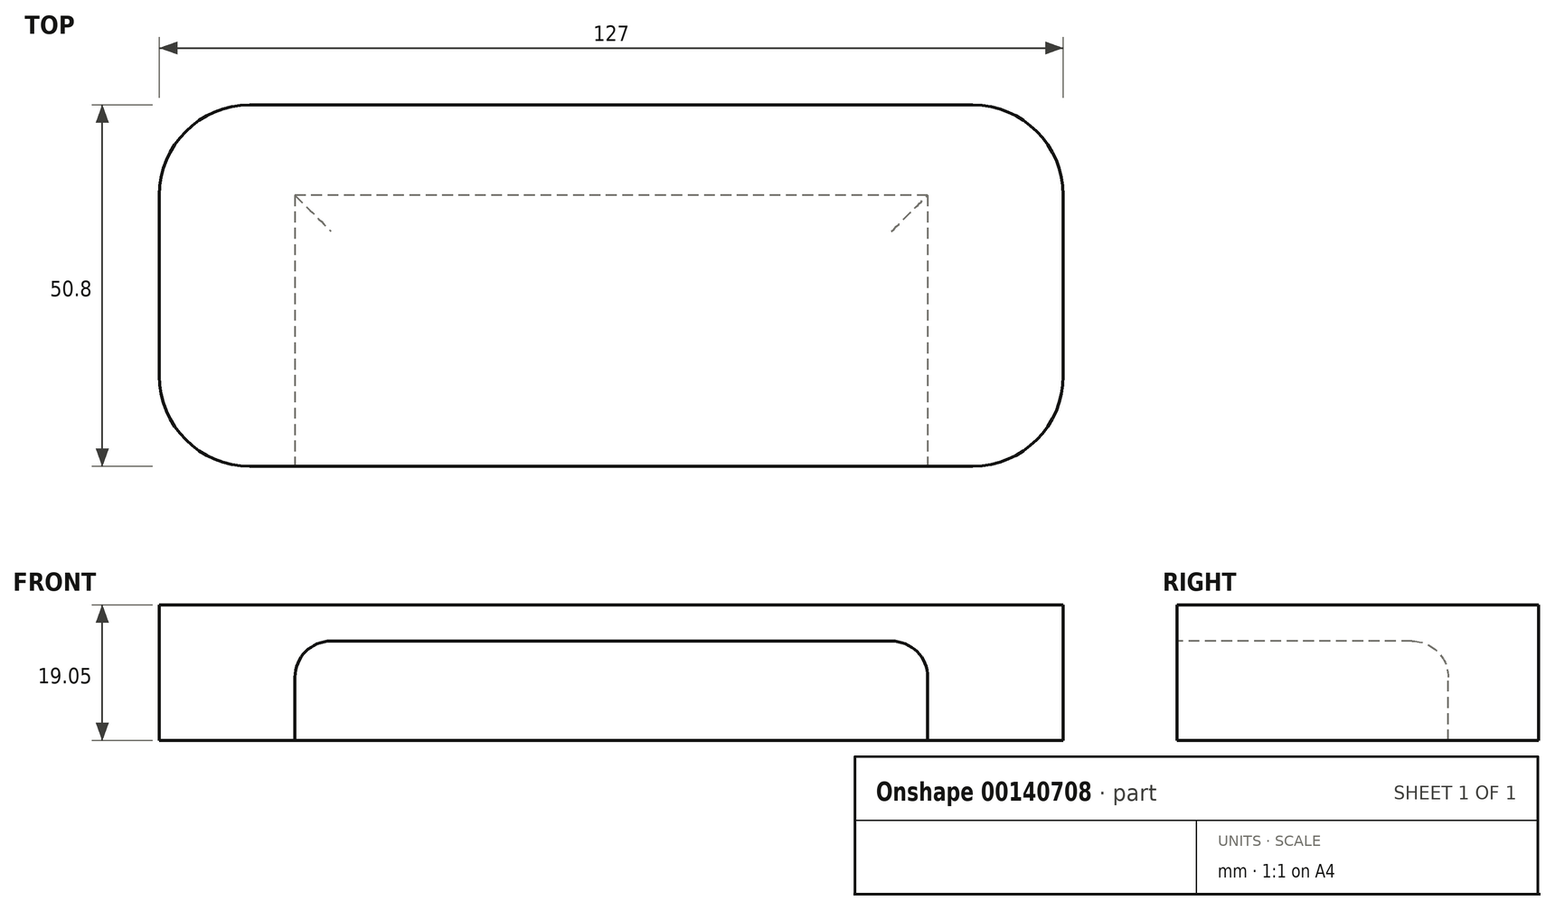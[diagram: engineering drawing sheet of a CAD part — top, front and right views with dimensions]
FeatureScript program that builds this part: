
annotation { "Feature Type Name" : "Feature", "Feature Type Description" : "" }
export const myFeature = defineFeature(function(context is Context, id is Id, definition is map)
    precondition{}
    {
        {
            var Q0;
            Q0=qCreatedBy(makeId("Top.planeOp"),FACE);
            var sketch = newSketch(context, id + "F0", { "sketchPlane" : qUnion([Q0])});
            skLineSegment(sketch, "E0.bottom", {"start": v(63.5, 25.4) * mm, "end": v(-63.5, 25.4) * mm});
            skLineSegment(sketch, "E0.top", {"start": v(63.5, -25.4) * mm, "end": v(-63.5, -25.4) * mm});
            skLineSegment(sketch, "E0.left", {"start": v(63.5, 25.4) * mm, "end": v(63.5, -25.4) * mm});
            skLineSegment(sketch, "E0.right", {"start": v(-63.5, 25.4) * mm, "end": v(-63.5, -25.4) * mm});
            skPoint(sketch, "E0.middle", {"position": v(0, 0) * mm});
            skSolve(sketch);
        }
        {
            var Q0;
            Q0 = qSketchRegion(id + "F0", true);
            extrude(context, id + "F1", {"entities" : qUnion([Q0]), "depth" : 19.05 * mm});
        }
        {
            var Q0;
            Q0=makeQuery(id+"F1.opExtrude","SWEPT_FACE",FACE,{"disambiguationData":[OSD([sQuery(id+"F0.wireOp",EDGE,"E0.top")])]});
            var sketch = newSketch(context, id + "F2", { "sketchPlane" : qUnion([Q0])});
            skLineSegment(sketch, "E1.bottom", {"start": v(-44.45, 0) * mm, "end": v(44.45, 0) * mm});
            skLineSegment(sketch, "E1.top", {"start": v(-44.45, 13.97) * mm, "end": v(44.45, 13.97) * mm});
            skLineSegment(sketch, "E1.left", {"start": v(-44.45, 0) * mm, "end": v(-44.45, 13.97) * mm});
            skLineSegment(sketch, "E1.right", {"start": v(44.45, 0) * mm, "end": v(44.45, 13.97) * mm});
            skSolve(sketch);
        }
        {
            var Q0;
            Q0 = qSketchRegion(id + "F2", true);
            extrude(context, id + "F3", {"entities" : qUnion([Q0]), "operationType" : NewBodyOperationType.REMOVE, "oppositeDirection" : true, "depth" : 38.1 * mm});
        }
        {
            var Q0;
            Q0=makeQuery(id+"F3.boolean.opBoolean","COPY",EDGE,{"derivedFrom":makeQuery(id+"F3.opExtrude","SWEPT_EDGE",EDGE,{"disambiguationData":[OSD([sQuery(id+"F2.wireOp",EDGE,"E1.top"),sQuery(id+"F2.wireOp",EDGE,"E1.right")])]})});
            var Q1;
            Q1=makeQuery(id+"F3.boolean.opBoolean","COPY",EDGE,{"derivedFrom":makeQuery(id+"F3.opExtrude","CAP_EDGE",EDGE,{"disambiguationData":[OSD([sQuery(id+"F2.wireOp",EDGE,"E1.top")])],"isStart":false})});
            var Q2;
            Q2=makeQuery(id+"F3.boolean.opBoolean","COPY",EDGE,{"derivedFrom":makeQuery(id+"F3.opExtrude","SWEPT_EDGE",EDGE,{"disambiguationData":[OSD([sQuery(id+"F2.wireOp",EDGE,"E1.top"),sQuery(id+"F2.wireOp",EDGE,"E1.left")])]})});
            fillet(context, id + "F4", {"entities" : qUnion([Q0, Q1, Q2]), "radius" : 5.08 * mm, "tangentPropagation" : true, "allowEdgeOverflow" : false});
        }
        {
            var Q0;
            Q0=makeQuery(id+"F1.opExtrude","SWEPT_EDGE",EDGE,{"disambiguationData":[OSD([sQuery(id+"F0.wireOp",EDGE,"E0.bottom"),sQuery(id+"F0.wireOp",EDGE,"E0.right")])]});
            var Q1;
            Q1=makeQuery(id+"F1.opExtrude","SWEPT_EDGE",EDGE,{"disambiguationData":[OSD([sQuery(id+"F0.wireOp",EDGE,"E0.bottom"),sQuery(id+"F0.wireOp",EDGE,"E0.left")])]});
            var Q2;
            Q2=makeQuery(id+"F1.opExtrude","SWEPT_EDGE",EDGE,{"disambiguationData":[OSD([sQuery(id+"F0.wireOp",EDGE,"E0.top"),sQuery(id+"F0.wireOp",EDGE,"E0.right")])]});
            var Q3;
            Q3=makeQuery(id+"F1.opExtrude","SWEPT_EDGE",EDGE,{"disambiguationData":[OSD([sQuery(id+"F0.wireOp",EDGE,"E0.top"),sQuery(id+"F0.wireOp",EDGE,"E0.left")])]});
            fillet(context, id + "F5", {"entities" : qUnion([Q0, Q1, Q2, Q3]), "radius" : 12.7 * mm, "tangentPropagation" : true, "allowEdgeOverflow" : false});
        }
    });
